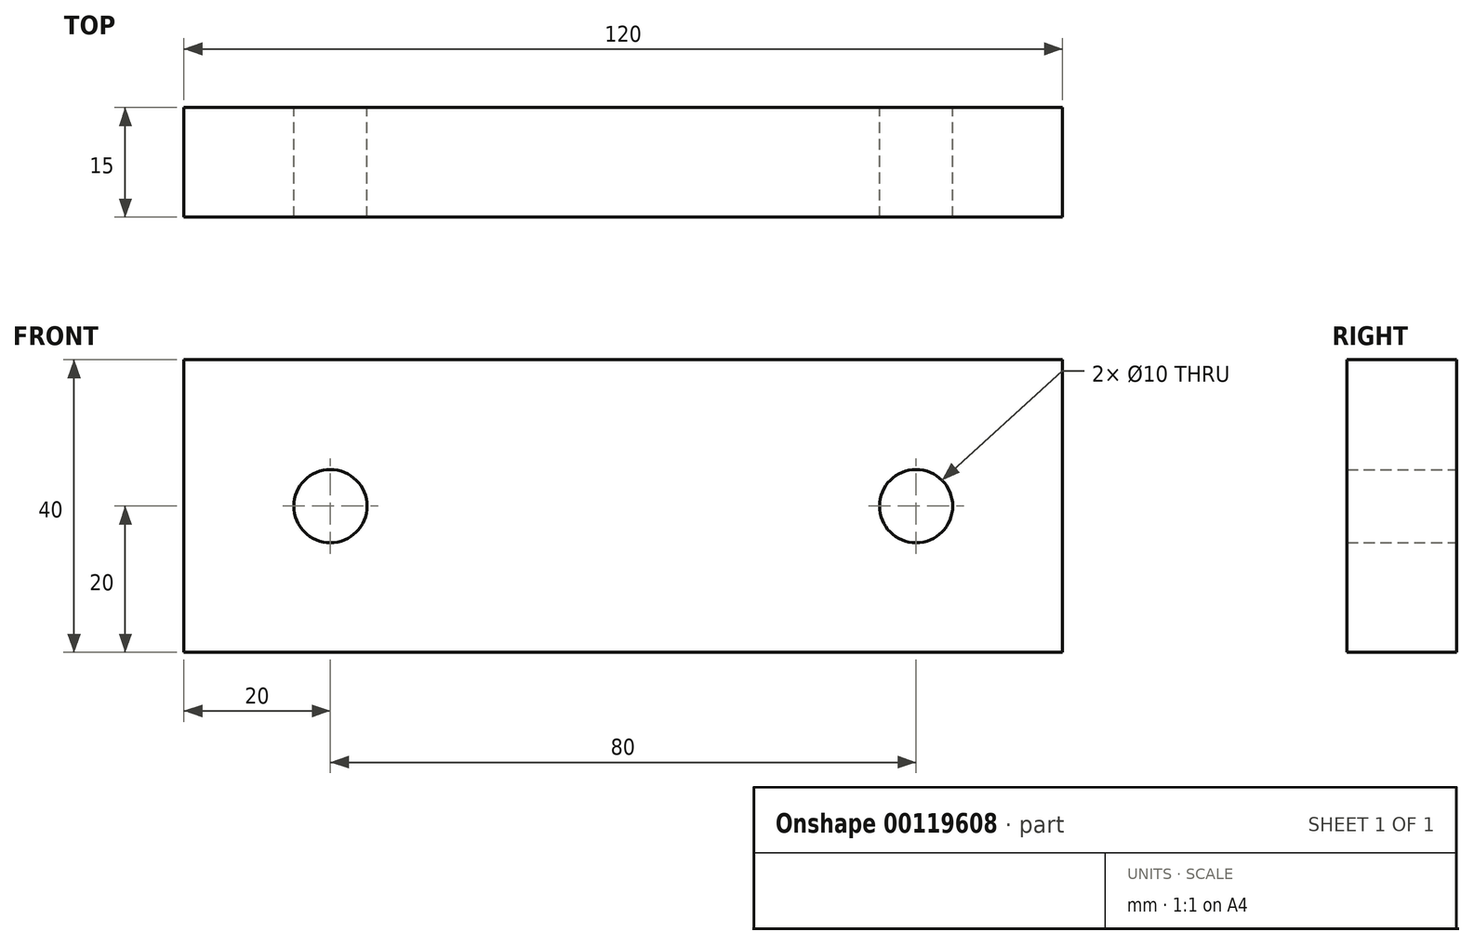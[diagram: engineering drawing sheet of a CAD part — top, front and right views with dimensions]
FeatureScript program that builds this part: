
annotation { "Feature Type Name" : "Feature", "Feature Type Description" : "" }
export const myFeature = defineFeature(function(context is Context, id is Id, definition is map)
    precondition{}
    {
        {
            var Q0;
            Q0=qCreatedBy(makeId("Front.planeOp"),FACE);
            var sketch = newSketch(context, id + "F0", { "sketchPlane" : qUnion([Q0])});
            skLineSegment(sketch, "E0.bottom", {"start": v(0, 40) * mm, "end": v(120, 40) * mm});
            skLineSegment(sketch, "E0.top", {"start": v(0, 0) * mm, "end": v(120, 0) * mm});
            skLineSegment(sketch, "E0.left", {"start": v(0, 40) * mm, "end": v(0, 0) * mm});
            skLineSegment(sketch, "E0.right", {"start": v(120, 40) * mm, "end": v(120, 0) * mm});
            skCircle(sketch, "E1", {"center": v(20, 20) * mm, "radius": 5 * mm});
            skCircle(sketch, "E2", {"center": v(100, 20) * mm, "radius": 5 * mm});
            skSolve(sketch);
        }
        {
            var Q0;
            Q0 = qSketchRegion(id + "F0", true);
            extrude(context, id + "F1", {"entities" : qUnion([Q0]), "depth" : 15 * mm});
        }
    });
